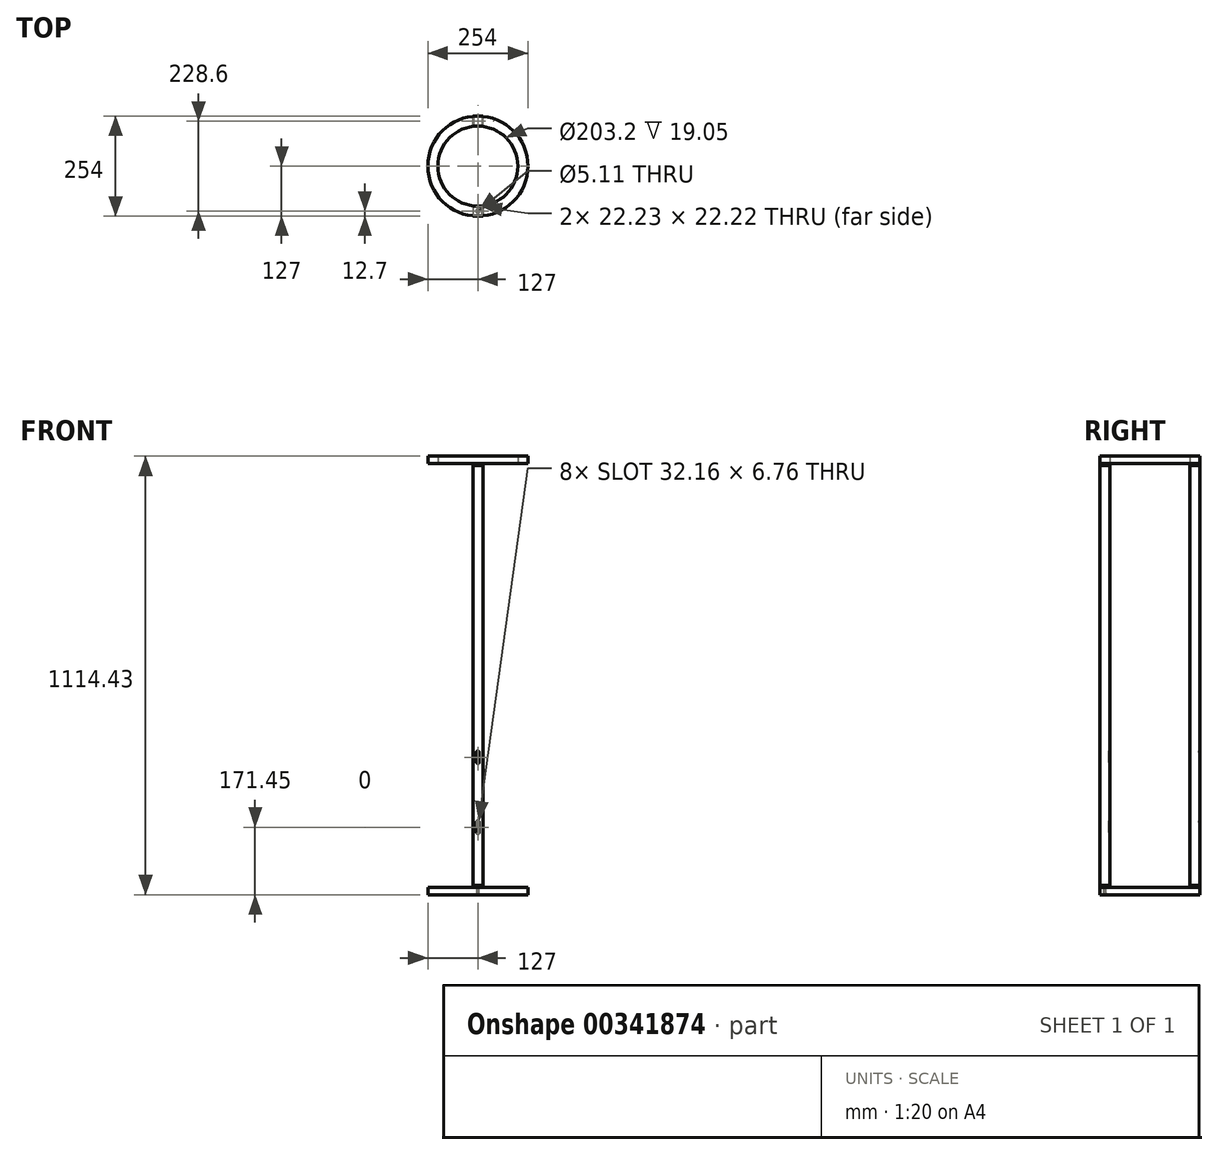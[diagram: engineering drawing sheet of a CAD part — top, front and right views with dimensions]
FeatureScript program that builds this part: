
annotation { "Feature Type Name" : "Feature", "Feature Type Description" : "" }
export const myFeature = defineFeature(function(context is Context, id is Id, definition is map)
    precondition{}
    {
        {
            var Q0;
            Q0=qCreatedBy(makeId("Top.planeOp"),FACE);
            var sketch = newSketch(context, id + "F0", { "sketchPlane" : qUnion([Q0])});
            skCircle(sketch, "E0", {"center": v(0, 0) * mm, "radius": 127 * mm});
            skSolve(sketch);
        }
        {
            var Q0;
            Q0 = qSketchRegion(id + "F0", true);
            extrude(context, id + "F1", {"entities" : qUnion([Q0]), "depth" : 19.05 * mm});
        }
        {
            var Q0;
            Q0=makeQuery(id+"F1.opExtrude","CAP_FACE",FACE,{"disambiguationData":[OSD([sQuery(id+"F0.wireOp",EDGE,"E0")])],"isStart":true});
            var sketch = newSketch(context, id + "F2", { "sketchPlane" : qUnion([Q0])});
            skPoint(sketch, "E1", {"position": v(0, 114.3) * mm});
            skSolve(sketch);
        }
        {
            var Q0;
            Q0=sQuery(id+"F2.wireOp",VERTEX,"E1");
            var Q1;
            Q1=makeQuery(id+"F1.opExtrude","SWEPT_BODY",BODY,{"disambiguationData":[OSD([sQuery(id+"F0.wireOp",EDGE,"E0")])]});
            hole(context, id + "F3", {"style" : HoleStyle.C_SINK, "endStyle" : HoleEndStyle.THROUGH, "standardTappedOrClearance" : lookupTablePath({ "standard" : "ANSI", "fit" : "Normal (ASME)", "size" : "#10", "type" : "Clearance" }), "standardBlindInLast" : lookupTablePath({ "fit" : "Free", "standard" : "ANSI", "size" : "#10", "type" : "Clearance" }), "holeDiameter" : 5.1 * mm, "cSinkDiameter" : 10.44 * mm, "cSinkAngle" : 82 * degree, "isTappedThrough" : true, "tappedDepth" : 12.7 * mm, "tapClearance" : 3, "locations" : qUnion([Q0]), "scope" : qUnion([Q1])});
        }
        {
            var Q0;
            Q0=makeQuery(id+"F1.opExtrude","CAP_FACE",FACE,{"disambiguationData":[OSD([sQuery(id+"F0.wireOp",EDGE,"E0")])],"isStart":false});
            var sketch = newSketch(context, id + "F4", { "sketchPlane" : qUnion([Q0])});
            skCircle(sketch, "E2", {"center": v(0, 0) * mm, "radius": 101.6 * mm});
            skSolve(sketch);
        }
        {
            var Q0;
            Q0=makeQuery(id+"F4.imprint","IMPRINT",FACE,{"disambiguationData":[TD([[makeQuery(id+"F4.imprint","IMPRINT",EDGE,{"derivedFrom":sQuery(id+"F4.wireOp",EDGE,"E2")}),-1.0]])]});
            var sketch = newSketch(context, id + "F5", { "sketchPlane" : qUnion([Q0])});
            skLineSegment(sketch, "E3.bottom", {"start": v(12.7, 101.6) * mm, "end": v(-12.7, 101.6) * mm});
            skLineSegment(sketch, "E3.top", {"start": v(12.7, 127) * mm, "end": v(-12.7, 127) * mm});
            skLineSegment(sketch, "E3.left", {"start": v(12.7, 101.6) * mm, "end": v(12.7, 127) * mm});
            skLineSegment(sketch, "E3.right", {"start": v(-12.7, 101.6) * mm, "end": v(-12.7, 127) * mm});
            skPoint(sketch, "E3.middle", {"position": v(0, 114.3) * mm});
            skSolve(sketch);
        }
        {
            var Q0;
            Q0 = qSketchRegion(id + "F5", true);
            extrude(context, id + "F6", {"entities" : qUnion([Q0]), "depth" : 4.76 * mm});
        }
        {
            var Q0;
            Q0=makeQuery(id+"F6.opExtrude","CAP_FACE",FACE,{"disambiguationData":[OSD([sQuery(id+"F5.wireOp",EDGE,"E3.bottom"),sQuery(id+"F5.wireOp",EDGE,"E3.top"),sQuery(id+"F5.wireOp",EDGE,"E3.left"),sQuery(id+"F5.wireOp",EDGE,"E3.right")])],"isStart":false});
            var sketch = newSketch(context, id + "F7", { "sketchPlane" : qUnion([Q0])});
            skLineSegment(sketch, "E4.bottom", {"start": v(12.7, 127) * mm, "end": v(-12.7, 127) * mm});
            skLineSegment(sketch, "E4.top", {"start": v(12.7, 101.6) * mm, "end": v(-12.7, 101.6) * mm});
            skLineSegment(sketch, "E4.left", {"start": v(12.7, 127) * mm, "end": v(12.7, 101.6) * mm});
            skLineSegment(sketch, "E4.right", {"start": v(-12.7, 127) * mm, "end": v(-12.7, 101.6) * mm});
            skLineSegment(sketch, "E5.0", {"start": v(11.11, 125.41) * mm, "end": v(11.11, 103.19) * mm});
            skLineSegment(sketch, "E5.1", {"start": v(11.11, 125.41) * mm, "end": v(-11.11, 125.41) * mm});
            skLineSegment(sketch, "E5.2", {"start": v(-11.11, 125.41) * mm, "end": v(-11.11, 103.19) * mm});
            skLineSegment(sketch, "E5.3", {"start": v(11.11, 103.19) * mm, "end": v(-11.11, 103.19) * mm});
            skSolve(sketch);
        }
        {
            var Q0;
            Q0 = qSketchRegion(id + "F7", true);
            extrude(context, id + "F8", {"entities" : qUnion([Q0]), "depth" : 1066.8 * mm});
        }
        {
            var Q0;
            Q0=makeQuery(id+"F8.opExtrude","CAP_FACE",FACE,{"disambiguationData":[OSD([sQuery(id+"F7.wireOp",EDGE,"E4.bottom"),sQuery(id+"F7.wireOp",EDGE,"E4.top"),sQuery(id+"F7.wireOp",EDGE,"E4.left"),sQuery(id+"F7.wireOp",EDGE,"E4.right"),sQuery(id+"F7.wireOp",EDGE,"E5.0"),sQuery(id+"F7.wireOp",EDGE,"E5.1"),sQuery(id+"F7.wireOp",EDGE,"E5.2"),sQuery(id+"F7.wireOp",EDGE,"E5.3")])],"isStart":true});
            var Q1;
            Q1=makeQuery(id+"F8.opExtrude","CAP_FACE",FACE,{"disambiguationData":[OSD([sQuery(id+"F7.wireOp",EDGE,"E4.bottom"),sQuery(id+"F7.wireOp",EDGE,"E4.top"),sQuery(id+"F7.wireOp",EDGE,"E4.left"),sQuery(id+"F7.wireOp",EDGE,"E4.right"),sQuery(id+"F7.wireOp",EDGE,"E5.0"),sQuery(id+"F7.wireOp",EDGE,"E5.1"),sQuery(id+"F7.wireOp",EDGE,"E5.2"),sQuery(id+"F7.wireOp",EDGE,"E5.3")])],"isStart":false});
            cPlane(context, id + "F9", {"entities" : qUnion([Q0, Q1]), "cplaneType" : CPlaneType.MID_PLANE, "offset" : 25.4 * mm, "width" : 152.4 * mm, "height" : 152.4 * mm});
        }
        {
            var Q0;
            Q0=makeQuery(id+"F6.opExtrude","SWEPT_BODY",BODY,{"disambiguationData":[OSD([sQuery(id+"F5.wireOp",EDGE,"E3.bottom"),sQuery(id+"F5.wireOp",EDGE,"E3.top"),sQuery(id+"F5.wireOp",EDGE,"E3.left"),sQuery(id+"F5.wireOp",EDGE,"E3.right")])]});
            var Q1;
            Q1=qCreatedBy(id+"F9.planeOp",FACE);
            mirror(context, id + "F10", {"entities" : qUnion([Q0]), "mirrorPlane" : qUnion([Q1])});
        }
        {
            var Q0;
            Q0=makeQuery(id+"F8.opExtrude","SWEPT_BODY",BODY,{"disambiguationData":[OSD([sQuery(id+"F7.wireOp",EDGE,"E4.bottom"),sQuery(id+"F7.wireOp",EDGE,"E4.top"),sQuery(id+"F7.wireOp",EDGE,"E4.left"),sQuery(id+"F7.wireOp",EDGE,"E4.right"),sQuery(id+"F7.wireOp",EDGE,"E5.0"),sQuery(id+"F7.wireOp",EDGE,"E5.1"),sQuery(id+"F7.wireOp",EDGE,"E5.2"),sQuery(id+"F7.wireOp",EDGE,"E5.3")])]});
            var Q1;
            Q1=makeQuery(id+"F10.opPattern","COPY",BODY,{"derivedFrom":makeQuery(id+"F6.opExtrude","SWEPT_BODY",BODY,{"disambiguationData":[OSD([sQuery(id+"F5.wireOp",EDGE,"E3.bottom"),sQuery(id+"F5.wireOp",EDGE,"E3.top"),sQuery(id+"F5.wireOp",EDGE,"E3.left"),sQuery(id+"F5.wireOp",EDGE,"E3.right")])]}),"instanceName":"1"});
            var Q2;
            Q2=makeQuery(id+"F6.opExtrude","SWEPT_BODY",BODY,{"disambiguationData":[OSD([sQuery(id+"F5.wireOp",EDGE,"E3.bottom"),sQuery(id+"F5.wireOp",EDGE,"E3.top"),sQuery(id+"F5.wireOp",EDGE,"E3.left"),sQuery(id+"F5.wireOp",EDGE,"E3.right")])]});
            var Q3;
            Q3=qCreatedBy(makeId("Front.planeOp"),FACE);
            mirror(context, id + "F11", {"entities" : qUnion([Q0, Q1, Q2]), "mirrorPlane" : qUnion([Q3])});
        }
        {
            var Q0;
            Q0=makeQuery(id+"F10.opPattern","COPY",FACE,{"derivedFrom":makeQuery(id+"F6.opExtrude","CAP_FACE",FACE,{"disambiguationData":[OSD([sQuery(id+"F5.wireOp",EDGE,"E3.bottom"),sQuery(id+"F5.wireOp",EDGE,"E3.top"),sQuery(id+"F5.wireOp",EDGE,"E3.left"),sQuery(id+"F5.wireOp",EDGE,"E3.right")])],"isStart":true}),"instanceName":"1"});
            var sketch = newSketch(context, id + "F12", { "sketchPlane" : qUnion([Q0])});
            skCircle(sketch, "E6", {"center": v(0, 0) * mm, "radius": 127 * mm});
            skCircle(sketch, "E7", {"center": v(0, 0) * mm, "radius": 101.6 * mm});
            skSolve(sketch);
        }
        {
            var Q0;
            {var subQ3=sQuery(id+"F12.wireOp",EDGE,"E7");Q0=makeQuery(id+"F12.imprint","IMPRINT",FACE,{"disambiguationData":[TD([[makeQuery(id+"F12.imprint","IMPRINT",EDGE,{"derivedFrom":subQ3}),-1.0]])]});}
            var Q1;
            {var subQ4=sQuery(id+"F12.wireOp",EDGE,"E6");var subQ5=makeQuery(id+"F12.imprint","INTERSECT",VERTEX,{"derivedFrom":[makeQuery(id+"F10.opPattern","COPY",EDGE,{"derivedFrom":makeQuery(id+"F6.opExtrude","CAP_EDGE",EDGE,{"disambiguationData":[OSD([sQuery(id+"F5.wireOp",EDGE,"E3.top")])],"isStart":true}),"instanceName":"1"}),subQ4]});Q1=makeQuery(id+"F12.imprint","IMPRINT",FACE,{"disambiguationData":[TD([[makeQuery(id+"F12.imprint","IMPRINT",EDGE,{"disambiguationData":[TD([[subQ5,1.0]])],"derivedFrom":subQ4}),1.0]])]});}
            extrude(context, id + "F13", {"entities" : qUnion([Q0, Q1]), "depth" : 19.05 * mm});
        }
        {
            var Q0;
            Q0=makeQuery(id+"F11.opPattern","COPY",FACE,{"derivedFrom":makeQuery(id+"F8.opExtrude","SWEPT_FACE",FACE,{"disambiguationData":[OSD([sQuery(id+"F7.wireOp",EDGE,"E4.bottom")])]}),"instanceName":"1"});
            var sketch = newSketch(context, id + "F14", { "sketchPlane" : qUnion([Q0])});
            skLineSegment(sketch, "E8", {"start": v(12.7, 349.25) * mm, "end": v(-12.7, 349.25) * mm, "construction": true});
            skLineSegment(sketch, "E9", {"start": v(12.7, 171.45) * mm, "end": v(-12.7, 171.45) * mm, "construction": true});
            skLineSegment(sketch, "E10", {"start": v(0, 361.95) * mm, "end": v(0, 336.55) * mm});
            skPoint(sketch, "E10.endSnap0", {"position": v(0, 349.25) * mm});
            skLineSegment(sketch, "E11", {"start": v(0, 184.15) * mm, "end": v(0, 158.75) * mm});
            skPoint(sketch, "E12", {"position": v(0, 171.45) * mm});
            skArc(sketch, "E13.0.startCap", {"start": v(-3.38, 361.95) * mm, "mid": v(0, 365.33) * mm, "end": v(3.38, 361.95) * mm});
            skArc(sketch, "E13.0.endCap", {"start": v(3.38, 336.55) * mm, "mid": v(0, 333.17) * mm, "end": v(-3.38, 336.55) * mm});
            skLineSegment(sketch, "E13.0.left", {"start": v(3.38, 361.95) * mm, "end": v(3.38, 336.55) * mm});
            skLineSegment(sketch, "E13.0.right", {"start": v(-3.38, 361.95) * mm, "end": v(-3.38, 336.55) * mm});
            skArc(sketch, "E13.1.startCap", {"start": v(-3.38, 184.15) * mm, "mid": v(0, 187.53) * mm, "end": v(3.38, 184.15) * mm});
            skArc(sketch, "E13.1.endCap", {"start": v(3.38, 158.75) * mm, "mid": v(0, 155.37) * mm, "end": v(-3.38, 158.75) * mm});
            skLineSegment(sketch, "E13.1.left", {"start": v(3.38, 184.15) * mm, "end": v(3.38, 158.75) * mm});
            skLineSegment(sketch, "E13.1.right", {"start": v(-3.38, 184.15) * mm, "end": v(-3.38, 158.75) * mm});
            skSolve(sketch);
        }
        {
            var Q0;
            Q0 = qSketchRegion(id + "F14", true);
            extrude(context, id + "F15", {"entities" : qUnion([Q0]), "operationType" : NewBodyOperationType.REMOVE, "endBound" : BoundingType.THROUGH_ALL, "oppositeDirection" : true, "depth" : 25.4 * mm});
        }
    });
